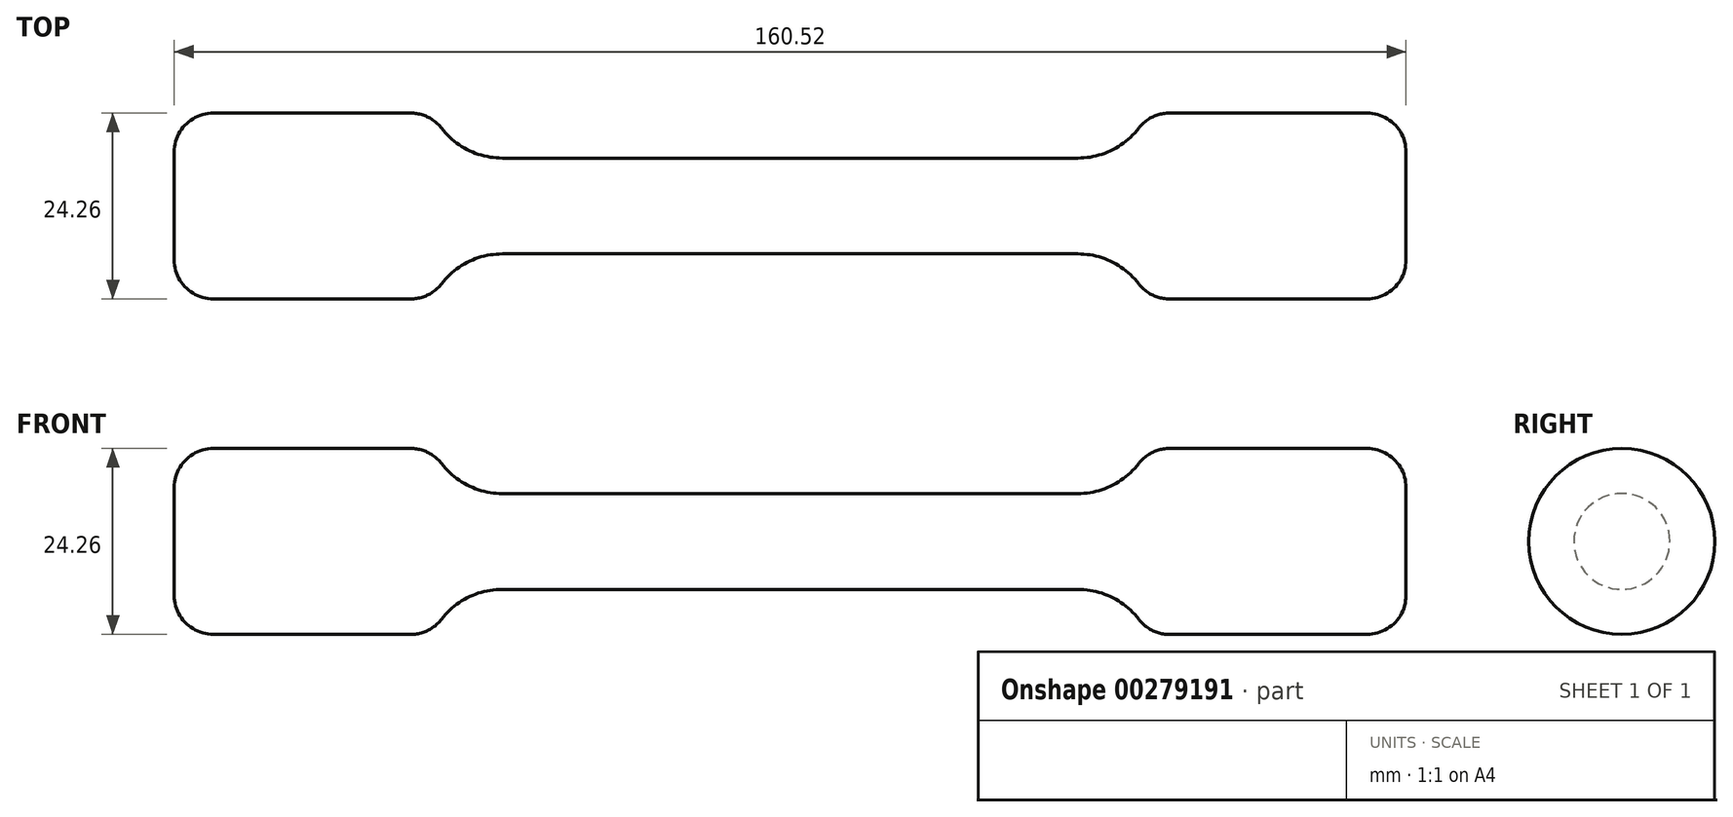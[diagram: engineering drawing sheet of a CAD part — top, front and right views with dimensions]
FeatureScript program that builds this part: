
annotation { "Feature Type Name" : "Feature", "Feature Type Description" : "" }
export const myFeature = defineFeature(function(context is Context, id is Id, definition is map)
    precondition{}
    {
        {
            var Q0;
            Q0=qCreatedBy(makeId("Front.planeOp"),FACE);
            var sketch = newSketch(context, id + "F0", { "sketchPlane" : qUnion([Q0])});
            skLineSegment(sketch, "E0", {"start": v(0, 6.25) * mm, "end": v(37.5, 6.25) * mm});
            skArc(sketch, "E1", {"start": v(37.5, 6.25) * mm, "mid": v(42.92, 7.85) * mm, "end": v(46.61, 12.13) * mm});
            skLineSegment(sketch, "E2", {"start": v(46.61, 12.13) * mm, "end": v(80.26, 12.13) * mm});
            skLineSegment(sketch, "E3", {"start": v(80.26, 12.13) * mm, "end": v(80.26, 0) * mm});
            skLineSegment(sketch, "E4.MirrorCS", {"start": v(0, 6.25) * mm, "end": v(-37.5, 6.25) * mm});
            skLineSegment(sketch, "E5.MirrorCS", {"start": v(-80.26, 12.13) * mm, "end": v(-80.26, 0) * mm});
            skLineSegment(sketch, "E6.MirrorCS", {"start": v(-46.61, 12.13) * mm, "end": v(-80.26, 12.13) * mm});
            skArc(sketch, "E7.MirrorCS", {"start": v(-37.5, 6.25) * mm, "mid": v(-42.92, 7.85) * mm, "end": v(-46.61, 12.13) * mm});
            skLineSegment(sketch, "E8", {"start": v(-80.26, 0) * mm, "end": v(80.26, 0) * mm});
            skSolve(sketch);
        }
        {
            var Q0;
            Q0=makeQuery(id+"F0.imprint","IMPRINT",FACE,{"disambiguationData":[TD([[makeQuery(id+"F0.imprint","IMPRINT",EDGE,{"derivedFrom":sQuery(id+"F0.wireOp",EDGE,"E0")}),-1.0]])]});
            var Q1;
            Q1=sQuery(id+"F0.wireOp",EDGE,"E8");
            revolve(context, id + "F1", {"entities" : qUnion([Q0]), "axis" : qUnion([Q1]), "revolveType" : RevolveType.FULL});
        }
        {
            var Q0;
            Q0=makeQuery(id+"F1.opRevolve","SWEPT_FACE",FACE,{"disambiguationData":[OSD([sQuery(id+"F0.wireOp",EDGE,"E7.MirrorCS")])]});
            var Q1;
            Q1=makeQuery(id+"F1.opRevolve","SWEPT_EDGE",EDGE,{"disambiguationData":[OSD([sQuery(id+"F0.wireOp",EDGE,"E1"),sQuery(id+"F0.wireOp",EDGE,"E2")])]});
            var Q2;
            Q2=makeQuery(id+"F1.opRevolve","SWEPT_EDGE",EDGE,{"disambiguationData":[OSD([sQuery(id+"F0.wireOp",EDGE,"E0"),sQuery(id+"F0.wireOp",EDGE,"E1")])]});
            var Q3;
            Q3=makeQuery(id+"F1.opRevolve","SWEPT_EDGE",EDGE,{"disambiguationData":[OSD([sQuery(id+"F0.wireOp",EDGE,"E5.MirrorCS"),sQuery(id+"F0.wireOp",EDGE,"E6.MirrorCS")])]});
            var Q4;
            Q4=makeQuery(id+"F1.opRevolve","SWEPT_FACE",FACE,{"disambiguationData":[OSD([sQuery(id+"F0.wireOp",EDGE,"E3")])]});
            fillet(context, id + "F2", {"entities" : qUnion([Q0, Q1, Q2, Q3, Q4]), "radius" : 5.08 * mm, "tangentPropagation" : true, "allowEdgeOverflow" : false});
        }
    });
